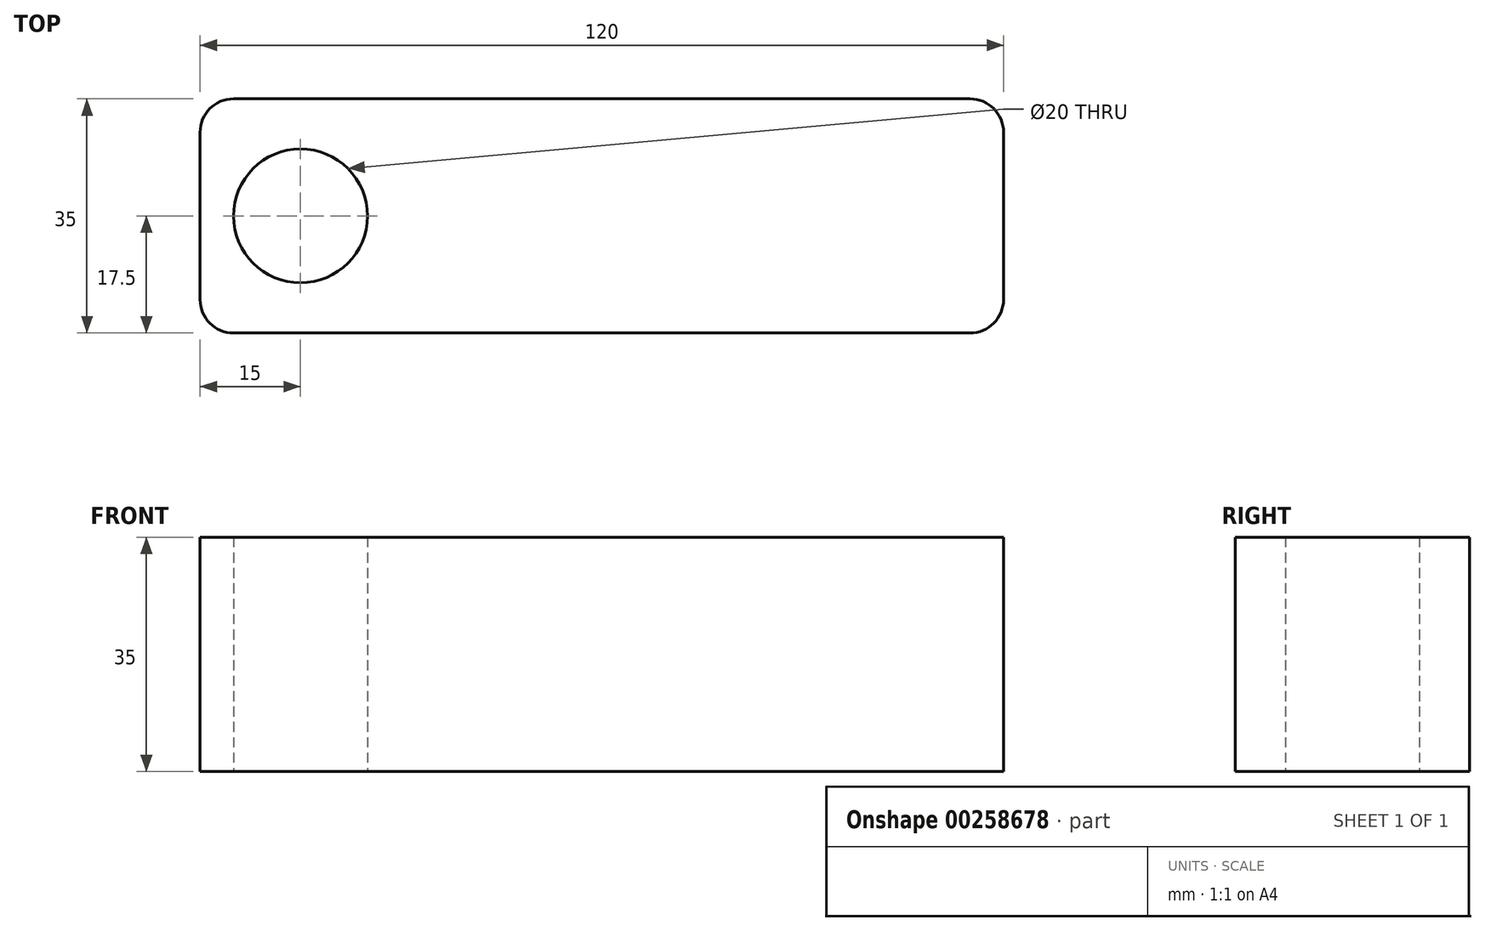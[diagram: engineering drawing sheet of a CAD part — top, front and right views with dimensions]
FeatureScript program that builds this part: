
annotation { "Feature Type Name" : "Feature", "Feature Type Description" : "" }
export const myFeature = defineFeature(function(context is Context, id is Id, definition is map)
    precondition{}
    {
        {
            var Q0;
            Q0=qCreatedBy(makeId("Top.planeOp"),FACE);
            var sketch = newSketch(context, id + "F0", { "sketchPlane" : qUnion([Q0])});
            skLineSegment(sketch, "E0.bottom", {"start": v(60, 17.5) * mm, "end": v(-60, 17.5) * mm});
            skLineSegment(sketch, "E0.top", {"start": v(60, -17.5) * mm, "end": v(-60, -17.5) * mm});
            skLineSegment(sketch, "E0.left", {"start": v(60, 17.5) * mm, "end": v(60, -17.5) * mm});
            skLineSegment(sketch, "E0.right", {"start": v(-60, 17.5) * mm, "end": v(-60, -17.5) * mm});
            skPoint(sketch, "E0.middle", {"position": v(0, 0) * mm});
            skCircle(sketch, "E1", {"center": v(-45, 0) * mm, "radius": 10 * mm});
            skSolve(sketch);
        }
        {
            var Q0;
            Q0=qSketchRegion(id+"F0",true);
            extrude(context, id + "F1", {"entities" : qUnion([Q0]), "depth" : 10 * mm});
        }
        {
            var Q0;
            Q0=makeQuery(id+"F1.opExtrude","SWEPT_EDGE",EDGE,{"disambiguationData":[OSD([sQuery(id+"F0.wireOp",EDGE,"E0.top"),sQuery(id+"F0.wireOp",EDGE,"E0.right")])]});
            var Q1;
            Q1=makeQuery(id+"F1.opExtrude","SWEPT_EDGE",EDGE,{"disambiguationData":[OSD([sQuery(id+"F0.wireOp",EDGE,"E0.top"),sQuery(id+"F0.wireOp",EDGE,"E0.left")])]});
            var Q2;
            Q2=makeQuery(id+"F1.opExtrude","SWEPT_EDGE",EDGE,{"disambiguationData":[OSD([sQuery(id+"F0.wireOp",EDGE,"E0.bottom"),sQuery(id+"F0.wireOp",EDGE,"E0.left")])]});
            var Q3;
            Q3=makeQuery(id+"F1.opExtrude","SWEPT_EDGE",EDGE,{"disambiguationData":[OSD([sQuery(id+"F0.wireOp",EDGE,"E0.bottom"),sQuery(id+"F0.wireOp",EDGE,"E0.right")])]});
            fillet(context, id + "F2", {"entities" : qUnion([Q0, Q1, Q2, Q3]), "radius" : 5 * mm, "tangentPropagation" : true, "allowEdgeOverflow" : false});
        }
        {
            var Q0;
            Q0=makeQuery(id+"F1.opExtrude","CAP_FACE",FACE,{"disambiguationData":[OSD([sQuery(id+"F0.wireOp",EDGE,"E0.bottom"),sQuery(id+"F0.wireOp",EDGE,"E0.top"),sQuery(id+"F0.wireOp",EDGE,"E0.left"),sQuery(id+"F0.wireOp",EDGE,"E0.right"),sQuery(id+"F0.wireOp",EDGE,"E1")])],"isStart":false});
            var sketch = newSketch(context, id + "F3", { "sketchPlane" : qUnion([Q0])});
            skLineSegment(sketch, "E2", {"start": v(-29.62, 17.5) * mm, "end": v(-29.62, -17.5) * mm, "construction": true});
            skSolve(sketch);
        }
        {
            var Q0;
            {var subQ0=sQuery(id+"F0.wireOp",EDGE,"E1");Q0=makeQuery(id+"F3.imprint","IMPRINT",FACE,{"disambiguationData":[TD([[makeQuery(id+"F3.imprint","IMPRINT",EDGE,{"derivedFrom":makeQuery(id+"F1.opExtrude","CAP_EDGE",EDGE,{"disambiguationData":[OSD([subQ0])],"isStart":false})}),-1.0]])]});}
            extrude(context, id + "F4", {"entities" : qUnion([Q0]), "operationType" : NewBodyOperationType.ADD, "depth" : 25 * mm});
        }
    });
